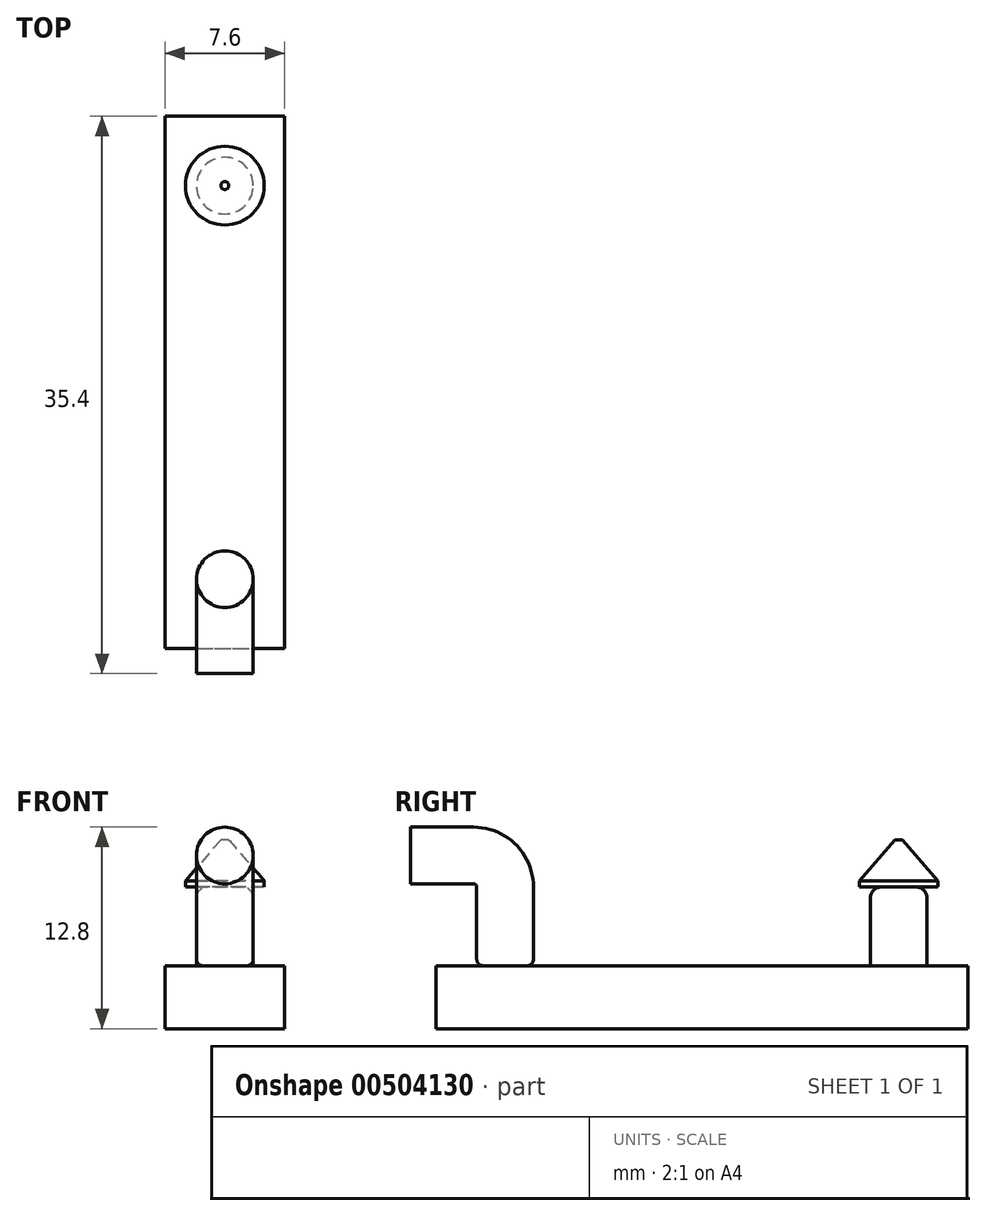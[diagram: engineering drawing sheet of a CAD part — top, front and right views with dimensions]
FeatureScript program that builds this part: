
annotation { "Feature Type Name" : "Feature", "Feature Type Description" : "" }
export const myFeature = defineFeature(function(context is Context, id is Id, definition is map)
    precondition{}
    {
        {
            var Q0;
            Q0=qCreatedBy(makeId("Top.planeOp"),FACE);
            var sketch = newSketch(context, id + "F0", { "sketchPlane" : qUnion([Q0])});
            skLineSegment(sketch, "E0.bottom", {"start": v(-3.8, 33.8) * mm, "end": v(3.8, 33.8) * mm});
            skLineSegment(sketch, "E0.top", {"start": v(-3.8, 0) * mm, "end": v(3.8, 0) * mm});
            skLineSegment(sketch, "E0.left", {"start": v(-3.8, 33.8) * mm, "end": v(-3.8, 0) * mm});
            skLineSegment(sketch, "E0.right", {"start": v(3.8, 33.8) * mm, "end": v(3.8, 0) * mm});
            skCircle(sketch, "E1", {"center": v(0, 29.4) * mm, "radius": 1.8 * mm});
            skPoint(sketch, "E1.centerSnap0", {"position": v(0, 33.8) * mm});
            skCircle(sketch, "E2", {"center": v(0, 4.4) * mm, "radius": 1.8 * mm});
            skPoint(sketch, "E2.centerSnap0", {"position": v(0, 0) * mm});
            skPoint(sketch, "E3", {"position": v(-9.75, 11.33) * mm});
            skSolve(sketch);
        }
        {
            var Q0;
            Q0=makeQuery(id+"F0.imprint","IMPRINT",FACE,{"disambiguationData":[TD([[makeQuery(id+"F0.imprint","IMPRINT",EDGE,{"derivedFrom":sQuery(id+"F0.wireOp",EDGE,"E1")}),1.0]])]});
            var Q1;
            Q1=makeQuery(id+"F0.imprint","IMPRINT",FACE,{"disambiguationData":[TD([[makeQuery(id+"F0.imprint","IMPRINT",EDGE,{"derivedFrom":sQuery(id+"F0.wireOp",EDGE,"E2")}),1.0]])]});
            extrude(context, id + "F1", {"entities" : qUnion([Q0, Q1]), "depth" : 5 * mm});
        }
        {
            var Q0;
            Q0=makeQuery(id+"F0.imprint","IMPRINT",FACE,{"disambiguationData":[TD([[makeQuery(id+"F0.imprint","IMPRINT",EDGE,{"derivedFrom":sQuery(id+"F0.wireOp",EDGE,"E0.bottom")}),-1.0]])]});
            var Q1;
            Q1=makeQuery(id+"F0.imprint","IMPRINT",FACE,{"disambiguationData":[TD([[makeQuery(id+"F0.imprint","IMPRINT",EDGE,{"derivedFrom":sQuery(id+"F0.wireOp",EDGE,"E1")}),1.0]])]});
            var Q2;
            Q2=makeQuery(id+"F0.imprint","IMPRINT",FACE,{"disambiguationData":[TD([[makeQuery(id+"F0.imprint","IMPRINT",EDGE,{"derivedFrom":sQuery(id+"F0.wireOp",EDGE,"E2")}),1.0]])]});
            extrude(context, id + "F2", {"entities" : qUnion([Q0, Q1, Q2]), "oppositeDirection" : true, "depth" : 4 * mm});
        }
        {
            var Q0;
            Q0=makeQuery(id+"F1.opExtrude","CAP_FACE",FACE,{"disambiguationData":[OSD([sQuery(id+"F0.wireOp",EDGE,"E1")])],"isStart":false});
            var sketch = newSketch(context, id + "F3", { "sketchPlane" : qUnion([Q0])});
            skCircle(sketch, "E4", {"center": v(0, 29.4) * mm, "radius": 2.5 * mm});
            skSolve(sketch);
        }
        {
            var Q0;
            Q0=makeQuery(id+"F3.imprint","IMPRINT",FACE,{"disambiguationData":[TD([[makeQuery(id+"F3.imprint","IMPRINT",EDGE,{"derivedFrom":sQuery(id+"F3.wireOp",EDGE,"E4")}),1.0]])]});
            cPlane(context, id + "F4", {"entities" : qUnion([Q0]), "cplaneType" : CPlaneType.OFFSET, "offset" : 3 * mm, "width" : 150 * mm, "height" : 150 * mm});
        }
        {
            var Q0;
            Q0=qCreatedBy(id+"F4.planeOp",FACE);
            var sketch = newSketch(context, id + "F5", { "sketchPlane" : qUnion([Q0])});
            skCircle(sketch, "E5", {"center": v(0, 29.4) * mm, "radius": 0.25 * mm});
            skSolve(sketch);
        }
        {
            var Q0;
            Q0=makeQuery(id+"F3.imprint","IMPRINT",FACE,{"disambiguationData":[TD([[makeQuery(id+"F3.imprint","IMPRINT",EDGE,{"derivedFrom":makeQuery(id+"F1.opExtrude","CAP_EDGE",EDGE,{"disambiguationData":[OSD([sQuery(id+"F0.wireOp",EDGE,"E1")])],"isStart":false})}),1.0]])]});
            var Q1;
            Q1=makeQuery(id+"F3.imprint","IMPRINT",FACE,{"disambiguationData":[TD([[makeQuery(id+"F3.imprint","IMPRINT",EDGE,{"derivedFrom":sQuery(id+"F3.wireOp",EDGE,"E4")}),1.0]])]});
            extrude(context, id + "F6", {"entities" : qUnion([Q0, Q1]), "depth" : 0.4 * mm});
        }
        {
            var Q0;
            Q0=makeQuery(id+"F6.opExtrude","CAP_FACE",FACE,{"disambiguationData":[OSD([sQuery(id+"F3.wireOp",EDGE,"E4")])],"isStart":false});
            var Q1;
            Q1=makeQuery(id+"F5.imprint","IMPRINT",FACE,{"disambiguationData":[TD([[makeQuery(id+"F5.imprint","IMPRINT",EDGE,{"derivedFrom":sQuery(id+"F5.wireOp",EDGE,"E5")}),1.0]])]});
            loft(context, id + "F7", {"sheetProfilesArray" : [{ "sheetProfileEntities" : qUnion([Q0]) }, { "sheetProfileEntities" : qUnion([Q1]) }]});
        }
        {
            var Q0;
            Q0=makeQuery(id+"F1.opExtrude","CAP_EDGE",EDGE,{"disambiguationData":[OSD([sQuery(id+"F0.wireOp",EDGE,"E1")])],"isStart":false});
            fillet(context, id + "F8", {"entities" : qUnion([Q0]), "radius" : 0.7 * mm, "tangentPropagation" : true, "allowEdgeOverflow" : false});
        }
        {
            var Q0;
            Q0=makeQuery(id+"F1.opExtrude","CAP_EDGE",EDGE,{"disambiguationData":[OSD([sQuery(id+"F0.wireOp",EDGE,"E2")])],"isStart":true});
            fillet(context, id + "F9", {"entities" : qUnion([Q0]), "radius" : 0.4 * mm, "tangentPropagation" : true, "allowEdgeOverflow" : false});
        }
        {
            var Q0;
            Q0=makeQuery(id+"F1.opExtrude","CAP_FACE",FACE,{"disambiguationData":[OSD([sQuery(id+"F0.wireOp",EDGE,"E2")])],"isStart":false});
            var sketch = newSketch(context, id + "F10", { "sketchPlane" : qUnion([Q0])});
            skCircle(sketch, "E6", {"center": v(0, 4.4) * mm, "radius": 1.8 * mm});
            skSolve(sketch);
        }
        {
            var Q0;
            Q0=qCreatedBy(makeId("Right.planeOp"),FACE);
            var sketch = newSketch(context, id + "F11", { "sketchPlane" : qUnion([Q0])});
            skLineSegment(sketch, "E7", {"start": v(4.4, 5) * mm, "end": v(4.4, 5) * mm});
            skLineSegment(sketch, "E8", {"start": v(2.4, 7) * mm, "end": v(-1.6, 7) * mm});
            skPoint(sketch, "E9.visualSharp", {"position": v(4.4, 7) * mm});
            skArc(sketch, "E9.filletArc", {"start": v(4.4, 5) * mm, "mid": v(3.81, 6.41) * mm, "end": v(2.4, 7) * mm});
            skSolve(sketch);
        }
        {
            var Q0;
            Q0=makeQuery(id+"F10.imprint","IMPRINT",FACE,{"disambiguationData":[TD([[makeQuery(id+"F10.imprint","IMPRINT",EDGE,{"derivedFrom":sQuery(id+"F10.wireOp",EDGE,"E6")}),1.0]])]});
            var Q1;
            Q1=sQuery(id+"F11.wireOp",EDGE,"E7");
            var Q2;
            Q2=sQuery(id+"F11.wireOp",EDGE,"E9.filletArc");
            var Q3;
            Q3=sQuery(id+"F11.wireOp",EDGE,"E8");
            sweep(context, id + "F12", {"operationType" : NewBodyOperationType.ADD, "profiles" : qUnion([Q0]), "path" : qUnion([Q1, Q2, Q3])});
        }
    });
